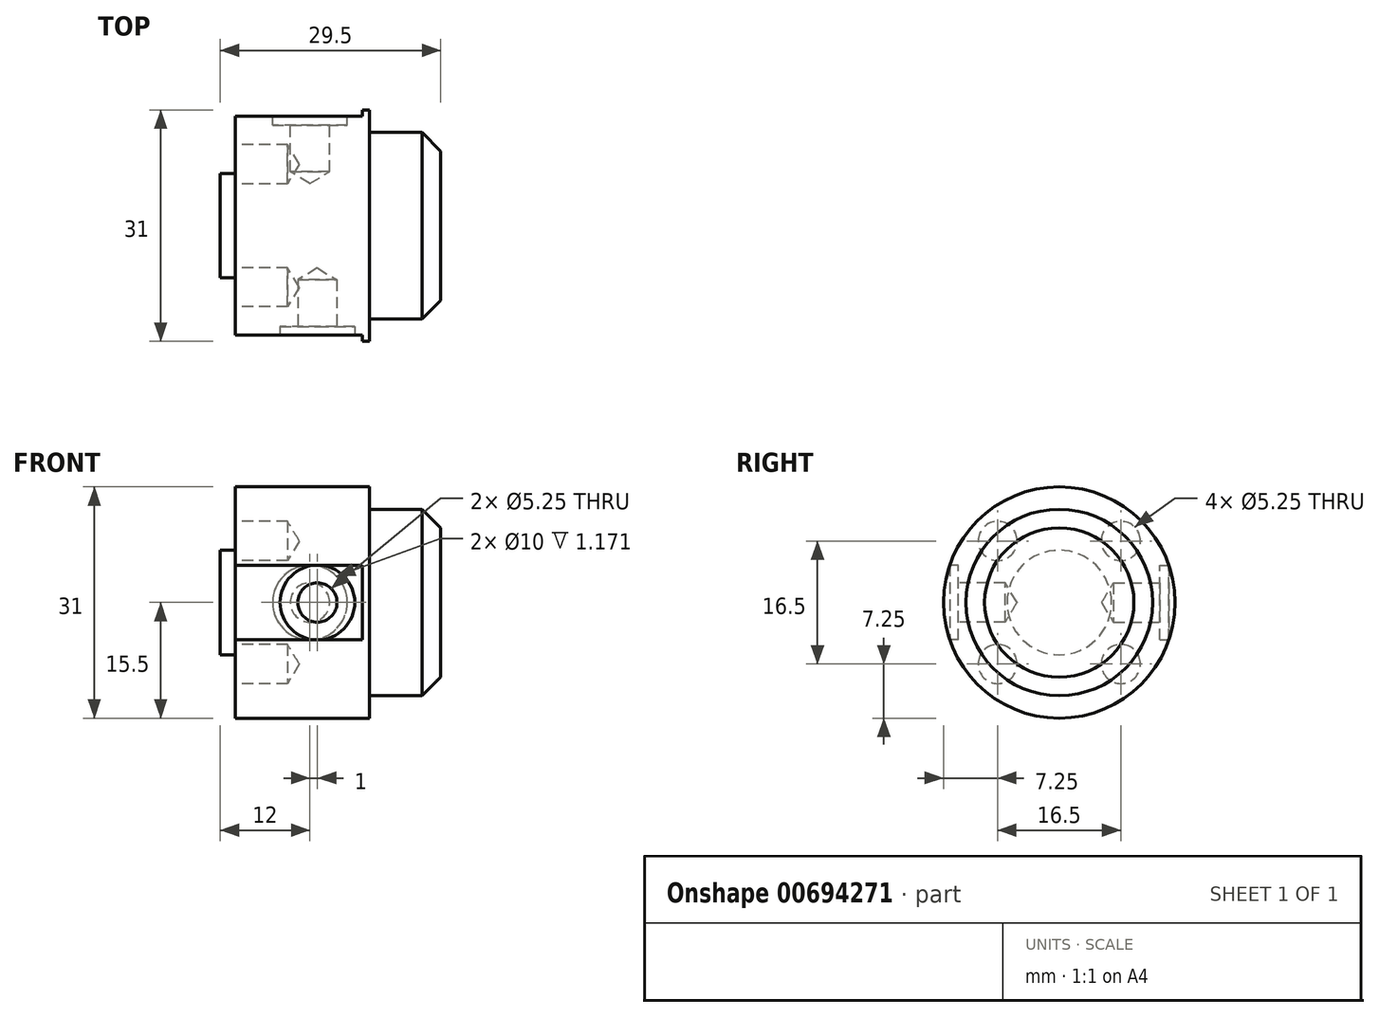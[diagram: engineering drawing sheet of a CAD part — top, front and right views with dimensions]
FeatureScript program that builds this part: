
annotation { "Feature Type Name" : "Feature", "Feature Type Description" : "" }
export const myFeature = defineFeature(function(context is Context, id is Id, definition is map)
    precondition{}
    {
        {
            var Q0;
            Q0=qCreatedBy(makeId("Front.planeOp"),FACE);
            var sketch = newSketch(context, id + "F0", { "sketchPlane" : qUnion([Q0])});
            skLineSegment(sketch, "E0", {"start": v(0, 5) * mm, "end": v(0, 15.5) * mm});
            skLineSegment(sketch, "E1", {"start": v(0, 15.5) * mm, "end": v(-18, 15.5) * mm});
            skLineSegment(sketch, "E2", {"start": v(-18, 15.5) * mm, "end": v(-18, 7) * mm});
            skLineSegment(sketch, "E3", {"start": v(-18, 7) * mm, "end": v(-20, 7) * mm});
            skLineSegment(sketch, "E4", {"start": v(-20, 7) * mm, "end": v(-20, 5) * mm});
            skPoint(sketch, "E5.startSnap0", {"position": v(0, 7.75) * mm});
            skPoint(sketch, "E6.end.orphan", {"position": v(0, 0) * mm});
            skPoint(sketch, "E7.orphan", {"position": v(-20, 0) * mm});
            skLineSegment(sketch, "E8", {"start": v(0, 0) * mm, "end": v(-10.6, 0) * mm, "construction": true});
            skLineSegment(sketch, "E9", {"start": v(-20, 5) * mm, "end": v(-20, 0) * mm});
            skLineSegment(sketch, "E10", {"start": v(0, 5) * mm, "end": v(0, 0) * mm});
            skLineSegment(sketch, "E11", {"start": v(-20, 0) * mm, "end": v(0, 0) * mm});
            skSolve(sketch);
        }
        {
            var Q0;
            Q0=qSketchRegion(id+"F0",true);
            var Q1;
            Q1=sQuery(id+"F0.wireOp",EDGE,"E8");
            revolve(context, id + "F1", {"entities" : qUnion([Q0]), "axis" : qUnion([Q1]), "revolveType" : RevolveType.FULL});
        }
        {
            var Q0;
            Q0=makeQuery(id+"F1.opRevolve","SWEPT_FACE",FACE,{"disambiguationData":[OSD([sQuery(id+"F0.wireOp",EDGE,"E2")])]});
            var sketch = newSketch(context, id + "F2", { "sketchPlane" : qUnion([Q0])});
            skCircle(sketch, "E12", {"center": v(8.25, 8.25) * mm, "radius": 1.5 * mm});
            skCircle(sketch, "E13.1.0", {"center": v(-8.25, 8.25) * mm, "radius": 1.5 * mm});
            skCircle(sketch, "E13.2.0", {"center": v(-8.25, -8.25) * mm, "radius": 1.5 * mm});
            skCircle(sketch, "E13.3.0", {"center": v(8.25, -8.25) * mm, "radius": 1.5 * mm});
            skPoint(sketch, "E13.center", {"position": v(0, 0) * mm});
            skSolve(sketch);
        }
        {
            var Q0;
            Q0=qSketchRegion(id+"F2",true);
            extrude(context, id + "F3", {"entities" : qUnion([Q0]), "operationType" : NewBodyOperationType.REMOVE, "oppositeDirection" : true, "depth" : 5 * mm, "offsetDistance" : 25 * mm});
        }
        {
            var Q0;
            Q0=makeQuery(id+"F1.opRevolve","SWEPT_FACE",FACE,{"disambiguationData":[OSD([sQuery(id+"F0.wireOp",EDGE,"E2")])]});
            var sketch = newSketch(context, id + "F4", { "sketchPlane" : qUnion([Q0])});
            skCircle(sketch, "E14", {"center": v(-8.25, 8.25) * mm, "radius": 0.94 * mm});
            skCircle(sketch, "E15.1.0", {"center": v(-8.25, -8.25) * mm, "radius": 0.94 * mm});
            skCircle(sketch, "E15.2.0", {"center": v(8.25, -8.25) * mm, "radius": 0.94 * mm});
            skCircle(sketch, "E15.3.0", {"center": v(8.25, 8.25) * mm, "radius": 0.94 * mm});
            skPoint(sketch, "E15.center", {"position": v(0, 0) * mm});
            skSolve(sketch);
        }
        {
            var Q0;
            Q0=sQuery(id+"F4.wireOp",VERTEX,"E14.center");
            var Q1;
            Q1=sQuery(id+"F4.wireOp",VERTEX,"E15.3.0.center");
            var Q2;
            Q2=sQuery(id+"F4.wireOp",VERTEX,"E15.1.0.center");
            var Q3;
            Q3=sQuery(id+"F4.wireOp",VERTEX,"E15.2.0.center");
            var Q4;
            Q4=makeQuery(id+"F1.opRevolve","SWEPT_BODY",BODY,{"disambiguationData":[OSD([sQuery(id+"F0.wireOp",EDGE,"E0"),sQuery(id+"F0.wireOp",EDGE,"E1"),sQuery(id+"F0.wireOp",EDGE,"E2"),sQuery(id+"F0.wireOp",EDGE,"E3"),sQuery(id+"F0.wireOp",EDGE,"E4"),sQuery(id+"F0.wireOp",EDGE,"E9"),sQuery(id+"F0.wireOp",EDGE,"E10"),sQuery(id+"F0.wireOp",EDGE,"E11")])]});
            hole(context, id + "F5", {"style" : HoleStyle.SIMPLE, "endStyle" : HoleEndStyle.BLIND, "standardTappedOrClearance" : lookupTablePath({ "standard" : "ISO", "engagement" : "75%", "pitch" : "0.75 mm", "size" : "M6", "type" : "Tapped" }), "standardBlindInLast" : lookupTablePath({ "standard" : "ISO", "engagement" : "75%", "pitch" : "0.75 mm", "size" : "M6", "type" : "Tapped" }), "holeDiameter" : 5.25 * mm, "majorDiameter" : 6 * mm, "showTappedDepth" : true, "holeDepth" : 7 * mm, "isTappedThrough" : true, "tappedDepth" : 6.25 * mm, "tapClearance" : 1, "locations" : qUnion([Q0, Q1, Q2, Q3]), "scope" : qUnion([Q4])});
        }
        {
            var Q0;
            Q0=qCreatedBy(makeId("Front.planeOp"),FACE);
            cPlane(context, id + "F6", {"entities" : qUnion([Q0]), "cplaneType" : CPlaneType.OFFSET, "offset" : 15.5 * mm, "width" : 150 * mm, "height" : 150 * mm});
        }
        {
            var Q0;
            Q0=qCreatedBy(id+"F6.planeOp",FACE);
            var sketch = newSketch(context, id + "F7", { "sketchPlane" : qUnion([Q0])});
            skCircle(sketch, "E16", {"center": v(-7, 0) * mm, "radius": 5 * mm});
            skSolve(sketch);
        }
        {
            var Q0;
            Q0=qSketchRegion(id+"F7",true);
            extrude(context, id + "F8", {"entities" : qUnion([Q0]), "operationType" : NewBodyOperationType.REMOVE, "oppositeDirection" : true, "depth" : 2 * mm, "offsetDistance" : 25 * mm});
        }
        {
            var Q0;
            Q0=makeQuery(id+"F8.boolean.opBoolean","COPY",FACE,{"derivedFrom":makeQuery(id+"F8.opExtrude","CAP_FACE",FACE,{"disambiguationData":[OSD([sQuery(id+"F7.wireOp",EDGE,"E16")])],"isStart":false})});
            var sketch = newSketch(context, id + "F9", { "sketchPlane" : qUnion([Q0])});
            skCircle(sketch, "E17", {"center": v(-7, 0) * mm, "radius": 2.73 * mm});
            skSolve(sketch);
        }
        {
            var Q0;
            Q0=sQuery(id+"F9.wireOp",VERTEX,"E17.center");
            var Q1;
            Q1=makeQuery(id+"F1.opRevolve","SWEPT_BODY",BODY,{"disambiguationData":[OSD([sQuery(id+"F0.wireOp",EDGE,"E0"),sQuery(id+"F0.wireOp",EDGE,"E1"),sQuery(id+"F0.wireOp",EDGE,"E2"),sQuery(id+"F0.wireOp",EDGE,"E3"),sQuery(id+"F0.wireOp",EDGE,"E4"),sQuery(id+"F0.wireOp",EDGE,"E9"),sQuery(id+"F0.wireOp",EDGE,"E10"),sQuery(id+"F0.wireOp",EDGE,"E11")])]});
            hole(context, id + "F10", {"style" : HoleStyle.SIMPLE, "endStyle" : HoleEndStyle.BLIND, "standardTappedOrClearance" : lookupTablePath({ "standard" : "ISO", "engagement" : "75%", "pitch" : "0.75 mm", "size" : "M6", "type" : "Tapped" }), "standardBlindInLast" : lookupTablePath({ "standard" : "ISO", "engagement" : "75%", "pitch" : "0.75 mm", "size" : "M6", "type" : "Tapped" }), "holeDiameter" : 5.25 * mm, "majorDiameter" : 6 * mm, "showTappedDepth" : true, "holeDepth" : 6.25 * mm, "isTappedThrough" : true, "tappedDepth" : 6.25 * mm, "tapClearance" : 0, "locations" : qUnion([Q0]), "scope" : qUnion([Q1])});
        }
        {
            var Q0;
            Q0=qCreatedBy(makeId("Front.planeOp"),FACE);
            cPlane(context, id + "F11", {"entities" : qUnion([Q0]), "cplaneType" : CPlaneType.OFFSET, "offset" : 15.5 * mm, "oppositeDirection" : true, "width" : 150 * mm, "height" : 150 * mm});
        }
        {
            var Q0;
            Q0=qCreatedBy(id+"F11.planeOp",FACE);
            var sketch = newSketch(context, id + "F12", { "sketchPlane" : qUnion([Q0])});
            skCircle(sketch, "E18", {"center": v(-8, 0) * mm, "radius": 5 * mm});
            skSolve(sketch);
        }
        {
            var Q0;
            Q0=qSketchRegion(id+"F12",true);
            extrude(context, id + "F13", {"entities" : qUnion([Q0]), "operationType" : NewBodyOperationType.REMOVE, "depth" : 2 * mm, "offsetDistance" : 25 * mm});
        }
        {
            var Q0;
            Q0=makeQuery(id+"F13.boolean.opBoolean","COPY",FACE,{"derivedFrom":makeQuery(id+"F13.opExtrude","CAP_FACE",FACE,{"disambiguationData":[OSD([sQuery(id+"F12.wireOp",EDGE,"E18")])],"isStart":false})});
            var sketch = newSketch(context, id + "F14", { "sketchPlane" : qUnion([Q0])});
            skCircle(sketch, "E19", {"center": v(8, 0) * mm, "radius": 1.83 * mm});
            skSolve(sketch);
        }
        {
            var Q0;
            Q0=sQuery(id+"F14.wireOp",VERTEX,"E19.center");
            var Q1;
            Q1=makeQuery(id+"F1.opRevolve","SWEPT_BODY",BODY,{"disambiguationData":[OSD([sQuery(id+"F0.wireOp",EDGE,"E0"),sQuery(id+"F0.wireOp",EDGE,"E1"),sQuery(id+"F0.wireOp",EDGE,"E2"),sQuery(id+"F0.wireOp",EDGE,"E3"),sQuery(id+"F0.wireOp",EDGE,"E4"),sQuery(id+"F0.wireOp",EDGE,"E9"),sQuery(id+"F0.wireOp",EDGE,"E10"),sQuery(id+"F0.wireOp",EDGE,"E11")])]});
            hole(context, id + "F15", {"style" : HoleStyle.SIMPLE, "endStyle" : HoleEndStyle.BLIND, "standardTappedOrClearance" : lookupTablePath({ "standard" : "ISO", "engagement" : "75%", "pitch" : "0.75 mm", "size" : "M6", "type" : "Tapped" }), "standardBlindInLast" : lookupTablePath({ "standard" : "ISO", "engagement" : "75%", "pitch" : "0.75 mm", "size" : "M6", "type" : "Tapped" }), "holeDiameter" : 5.25 * mm, "majorDiameter" : 6 * mm, "showTappedDepth" : true, "holeDepth" : 6.25 * mm, "isTappedThrough" : true, "tappedDepth" : 6.25 * mm, "tapClearance" : 0, "locations" : qUnion([Q0]), "scope" : qUnion([Q1])});
        }
        {
            var Q0;
            Q0=makeQuery(id+"F1.opRevolve","SWEPT_FACE",FACE,{"disambiguationData":[OSD([sQuery(id+"F0.wireOp",EDGE,"E0"),sQuery(id+"F0.wireOp",EDGE,"E10")])]});
            var sketch = newSketch(context, id + "F16", { "sketchPlane" : qUnion([Q0])});
            skCircle(sketch, "E20", {"center": v(0, 0) * mm, "radius": 12.5 * mm});
            skSolve(sketch);
        }
        {
            var Q0;
            Q0=qSketchRegion(id+"F16",true);
            extrude(context, id + "F17", {"entities" : qUnion([Q0]), "operationType" : NewBodyOperationType.ADD, "depth" : 9.5 * mm, "offsetDistance" : 25 * mm});
        }
        {
            var Q0;
            Q0=makeQuery(id+"F17.opExtrude","CAP_EDGE",EDGE,{"disambiguationData":[OSD([sQuery(id+"F16.wireOp",EDGE,"E20")])],"isStart":false});
            chamfer(context, id + "F18", {"entities" : qUnion([Q0]), "width" : 2.5 * mm, "tangentPropagation" : true});
        }
        {
            var Q0;
            Q0=makeQuery(id+"F1.opRevolve","SWEPT_FACE",FACE,{"disambiguationData":[OSD([sQuery(id+"F0.wireOp",EDGE,"E2")])]});
            var sketch = newSketch(context, id + "F19", { "sketchPlane" : qUnion([Q0])});
            skArc(sketch, "E21", {"start": v(-14.67, 5) * mm, "mid": v(-15.5, 0) * mm, "end": v(-14.67, -5) * mm});
            skLineSegment(sketch, "E22", {"start": v(14.67, 5) * mm, "end": v(14.67, -5) * mm});
            skLineSegment(sketch, "E23", {"start": v(-14.67, 5) * mm, "end": v(-14.67, -5) * mm});
            skArc(sketch, "E24.trimOffspring", {"start": v(14.67, -5) * mm, "mid": v(15.5, 0) * mm, "end": v(14.67, 5) * mm});
            skSolve(sketch);
        }
        {
            var Q0;
            Q0=qSketchRegion(id+"F19",true);
            extrude(context, id + "F20", {"entities" : qUnion([Q0]), "operationType" : NewBodyOperationType.REMOVE, "oppositeDirection" : true, "depth" : 17 * mm, "offsetDistance" : 25 * mm});
        }
    });
